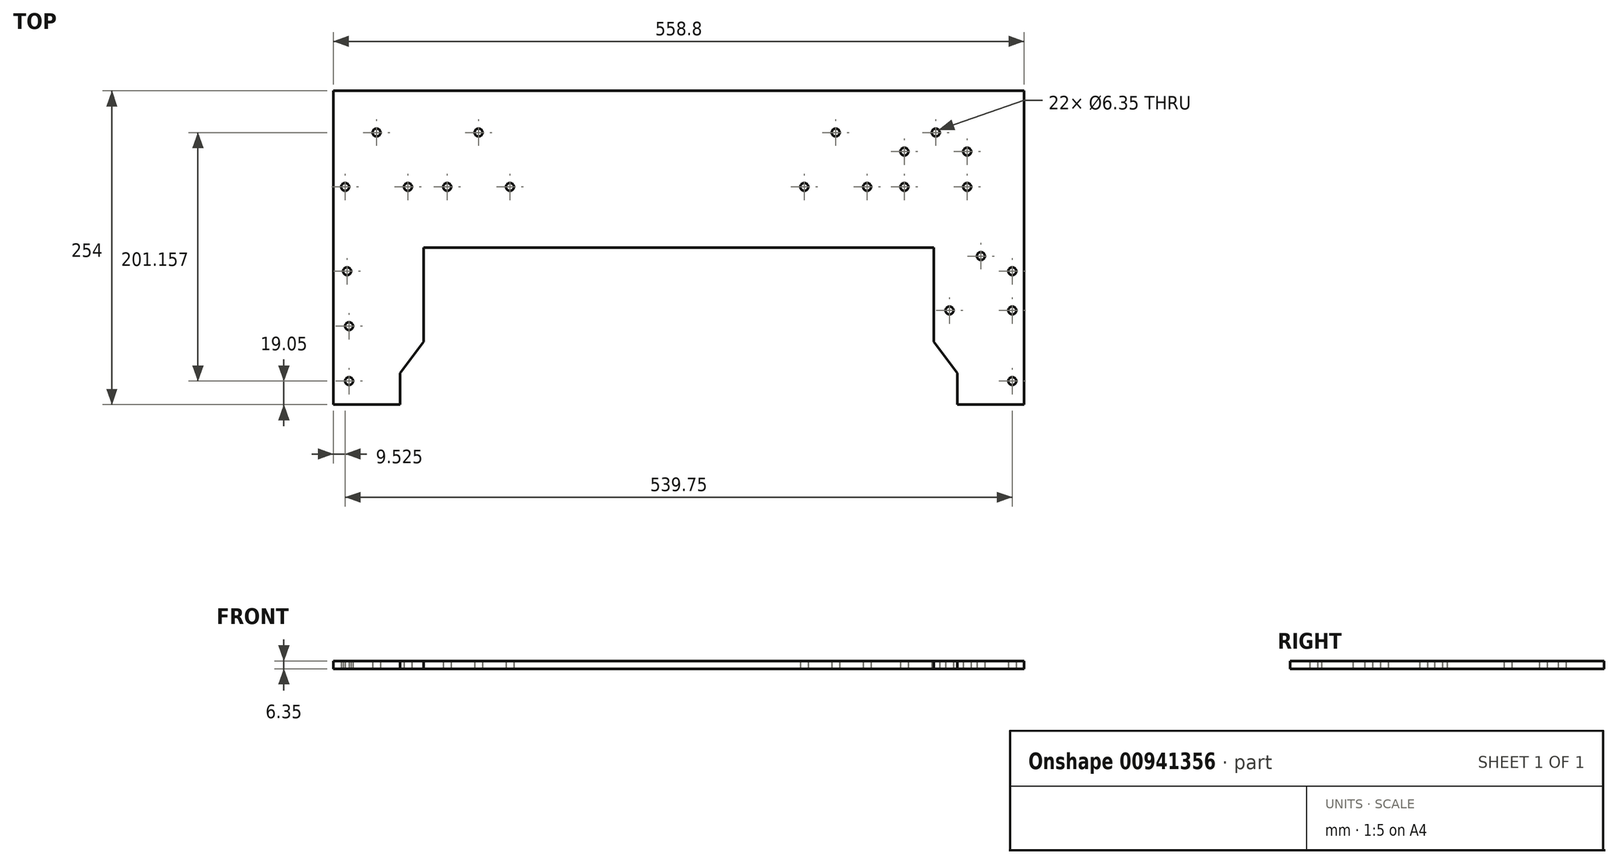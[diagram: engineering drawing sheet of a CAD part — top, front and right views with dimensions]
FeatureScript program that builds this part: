
annotation { "Feature Type Name" : "Feature", "Feature Type Description" : "" }
export const myFeature = defineFeature(function(context is Context, id is Id, definition is map)
    precondition{}
    {
        {
            var Q0;
            Q0=qCreatedBy(makeId("Top.planeOp"),FACE);
            var sketch = newSketch(context, id + "F0", { "sketchPlane" : qUnion([Q0])});
            skLineSegment(sketch, "E0", {"start": v(0, 0) * mm, "end": v(0, 254) * mm});
            skLineSegment(sketch, "E1", {"start": v(0, 254) * mm, "end": v(558.8, 254) * mm});
            skLineSegment(sketch, "E2", {"start": v(558.8, 254) * mm, "end": v(558.8, 0) * mm});
            skLineSegment(sketch, "E3", {"start": v(558.8, 0) * mm, "end": v(504.83, 0) * mm});
            skLineSegment(sketch, "E4", {"start": v(504.83, 0) * mm, "end": v(504.83, 25.4) * mm});
            skLineSegment(sketch, "E5", {"start": v(485.78, 50.8) * mm, "end": v(485.78, 127) * mm});
            skLineSegment(sketch, "E6", {"start": v(0, 0) * mm, "end": v(53.98, 0) * mm});
            skLineSegment(sketch, "E7", {"start": v(53.98, 0) * mm, "end": v(53.98, 25.4) * mm});
            skLineSegment(sketch, "E8", {"start": v(73.03, 50.8) * mm, "end": v(73.03, 127) * mm});
            skLineSegment(sketch, "E9", {"start": v(73.03, 127) * mm, "end": v(485.78, 127) * mm});
            skLineSegment(sketch, "E10", {"start": v(53.97, 25.4) * mm, "end": v(73.03, 50.8) * mm});
            skLineSegment(sketch, "E11", {"start": v(485.78, 50.8) * mm, "end": v(504.83, 25.4) * mm});
            skCircle(sketch, "E12", {"center": v(549.28, 19.05) * mm, "radius": 3.18 * mm});
            skCircle(sketch, "E13", {"center": v(549.28, 107.95) * mm, "radius": 3.18 * mm});
            skCircle(sketch, "E14", {"center": v(549.28, 76.2) * mm, "radius": 3.18 * mm});
            skCircle(sketch, "E15", {"center": v(498.48, 76.2) * mm, "radius": 3.18 * mm});
            skCircle(sketch, "E16", {"center": v(523.88, 120.2) * mm, "radius": 3.18 * mm});
            skCircle(sketch, "E17", {"center": v(512.76, 176.21) * mm, "radius": 3.18 * mm});
            skCircle(sketch, "E18", {"center": v(461.96, 176.21) * mm, "radius": 3.18 * mm});
            skCircle(sketch, "E19", {"center": v(487.36, 220.2) * mm, "radius": 3.18 * mm});
            skCircle(sketch, "E20", {"center": v(512.76, 204.79) * mm, "radius": 3.18 * mm});
            skCircle(sketch, "E21", {"center": v(461.96, 204.79) * mm, "radius": 3.18 * mm});
            skCircle(sketch, "E22", {"center": v(431.8, 176.21) * mm, "radius": 3.18 * mm});
            skCircle(sketch, "E23", {"center": v(381, 176.21) * mm, "radius": 3.18 * mm});
            skCircle(sketch, "E24", {"center": v(406.4, 220.2) * mm, "radius": 3.18 * mm});
            skCircle(sketch, "E25", {"center": v(9.53, 176.21) * mm, "radius": 3.18 * mm});
            skCircle(sketch, "E26", {"center": v(60.33, 176.21) * mm, "radius": 3.18 * mm});
            skCircle(sketch, "E27", {"center": v(34.92, 220.2) * mm, "radius": 3.18 * mm});
            skCircle(sketch, "E28", {"center": v(92.08, 176.21) * mm, "radius": 3.18 * mm});
            skCircle(sketch, "E29", {"center": v(142.88, 176.21) * mm, "radius": 3.18 * mm});
            skCircle(sketch, "E30", {"center": v(117.47, 220.2) * mm, "radius": 3.18 * mm});
            skCircle(sketch, "E31", {"center": v(12.7, 19.05) * mm, "radius": 3.18 * mm});
            skCircle(sketch, "E32", {"center": v(12.7, 63.5) * mm, "radius": 3.18 * mm});
            skCircle(sketch, "E33", {"center": v(11.11, 107.95) * mm, "radius": 3.18 * mm});
            skSolve(sketch);
        }
        {
            var Q0;
            Q0 = qSketchRegion(id + "F0", true);
            extrude(context, id + "F1", {"entities" : qUnion([Q0]), "depth" : 6.35 * mm, "offsetDistance" : 25.4 * mm});
        }
    });
